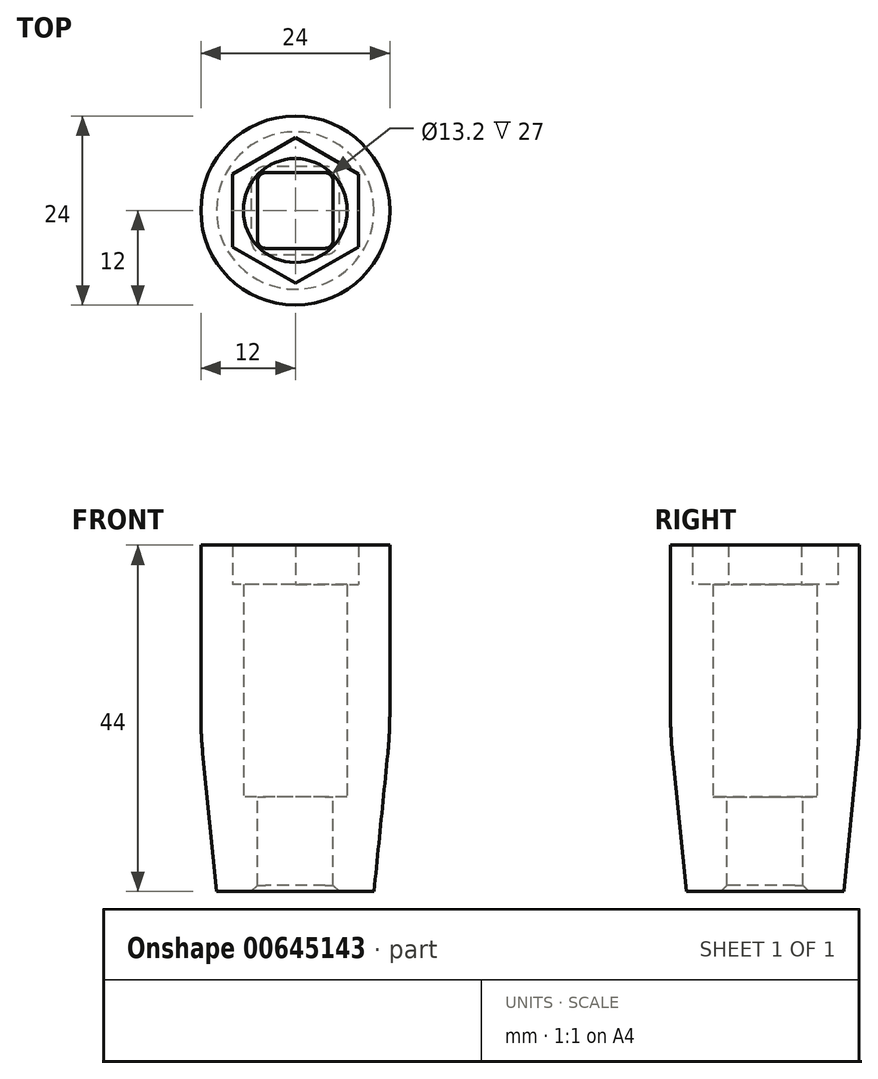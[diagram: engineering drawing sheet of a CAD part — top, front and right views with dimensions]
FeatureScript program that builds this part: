
annotation { "Feature Type Name" : "Feature", "Feature Type Description" : "" }
export const myFeature = defineFeature(function(context is Context, id is Id, definition is map)
    precondition{}
    {
        {
            var Q0;
            Q0=qCreatedBy(makeId("Top.planeOp"),FACE);
            var sketch = newSketch(context, id + "F0", { "sketchPlane" : qUnion([Q0])});
            skCircle(sketch, "E0.cCircle", {"center": v(0, 0) * mm, "radius": 8 * mm, "construction": true});
            skLineSegment(sketch, "E0.0", {"start": v(8, 4.62) * mm, "end": v(8, -4.62) * mm});
            skLineSegment(sketch, "E0.1", {"start": v(8, -4.62) * mm, "end": v(0, -9.24) * mm});
            skLineSegment(sketch, "E0.2", {"start": v(0, -9.24) * mm, "end": v(-8, -4.62) * mm});
            skLineSegment(sketch, "E0.3", {"start": v(-8, -4.62) * mm, "end": v(-8, 4.62) * mm});
            skLineSegment(sketch, "E0.4", {"start": v(-8, 4.62) * mm, "end": v(0, 9.24) * mm});
            skLineSegment(sketch, "E0.5", {"start": v(0, 9.24) * mm, "end": v(8, 4.62) * mm});
            skPoint(sketch, "E0.0.midPoint", {"position": v(8, 0) * mm});
            skCircle(sketch, "E1", {"center": v(0, 0) * mm, "radius": 12 * mm});
            skLineSegment(sketch, "E2.bottom", {"start": v(4.8, -4.8) * mm, "end": v(-4.8, -4.8) * mm});
            skLineSegment(sketch, "E2.top", {"start": v(4.8, 4.8) * mm, "end": v(-4.8, 4.8) * mm});
            skLineSegment(sketch, "E2.left", {"start": v(4.8, -4.8) * mm, "end": v(4.8, 4.8) * mm});
            skLineSegment(sketch, "E2.right", {"start": v(-4.8, -4.8) * mm, "end": v(-4.8, 4.8) * mm});
            skSolve(sketch);
        }
        {
            var Q0;
            {var subQ5=sQuery(id+"F0.wireOp",EDGE,"E0.0");Q0=makeQuery(id+"F0.imprint","IMPRINT",FACE,{"disambiguationData":[TD([[makeQuery(id+"F0.imprint","IMPRINT",EDGE,{"derivedFrom":subQ5}),1.0]])]});}
            var Q1;
            Q1=makeQuery(id+"F0.imprint","IMPRINT",FACE,{"disambiguationData":[TD([[makeQuery(id+"F0.imprint","IMPRINT",EDGE,{"derivedFrom":sQuery(id+"F0.wireOp",EDGE,"E1")}),-1.0]])]});
            extrude(context, id + "F1", {"entities" : qUnion([Q0, Q1]), "depth" : 32 * mm, "offsetDistance" : 25 * mm});
        }
        {
            var Q0;
            Q0=makeQuery(id+"F0.imprint","IMPRINT",FACE,{"disambiguationData":[TD([[makeQuery(id+"F0.imprint","IMPRINT",EDGE,{"derivedFrom":sQuery(id+"F0.wireOp",EDGE,"E0.0")}),-1.0]])]});
            var Q1;
            Q1=makeQuery(id+"F0.imprint","IMPRINT",FACE,{"disambiguationData":[TD([[makeQuery(id+"F0.imprint","IMPRINT",EDGE,{"derivedFrom":sQuery(id+"F0.wireOp",EDGE,"E0.0")}),1.0]])]});
            extrude(context, id + "F2", {"entities" : qUnion([Q0, Q1]), "operationType" : NewBodyOperationType.ADD, "oppositeDirection" : true, "depth" : 12 * mm, "offsetDistance" : 25 * mm});
        }
        {
            var Q0;
            Q0=makeQuery(id+"F2.opExtrude","CAP_EDGE",EDGE,{"disambiguationData":[OSD([sQuery(id+"F0.wireOp",EDGE,"E1")])],"isStart":false});
            chamfer(context, id + "F3", {"entities" : qUnion([Q0]), "chamferType" : ChamferType.TWO_OFFSETS, "width1" : 2 * mm, "oppositeDirection" : true, "width2" : 20 * mm, "tangentPropagation" : true});
        }
        {
            var Q0;
            Q0=makeQuery(id+"F2.opExtrude","SWEPT_EDGE",EDGE,{"disambiguationData":[OSD([sQuery(id+"F0.wireOp",EDGE,"E2.top"),sQuery(id+"F0.wireOp",EDGE,"E2.right")])]});
            var Q1;
            Q1=makeQuery(id+"F2.opExtrude","SWEPT_EDGE",EDGE,{"disambiguationData":[OSD([sQuery(id+"F0.wireOp",EDGE,"E2.top"),sQuery(id+"F0.wireOp",EDGE,"E2.left")])]});
            var Q2;
            Q2=makeQuery(id+"F2.opExtrude","SWEPT_EDGE",EDGE,{"disambiguationData":[OSD([sQuery(id+"F0.wireOp",EDGE,"E2.bottom"),sQuery(id+"F0.wireOp",EDGE,"E2.left")])]});
            var Q3;
            Q3=makeQuery(id+"F2.opExtrude","SWEPT_EDGE",EDGE,{"disambiguationData":[OSD([sQuery(id+"F0.wireOp",EDGE,"E2.bottom"),sQuery(id+"F0.wireOp",EDGE,"E2.right")])]});
            fillet(context, id + "F4", {"entities" : qUnion([Q0, Q1, Q2, Q3]), "tangentPropagation" : true, "radius" : 1 * mm, "defaultsChanged" : false, "vertexSettings" : [], "allowEdgeOverflow" : false});
        }
        {
            var Q0;
            Q0=makeQuery(id+"F0.imprint","IMPRINT",FACE,{"disambiguationData":[TD([[makeQuery(id+"F0.imprint","IMPRINT",EDGE,{"derivedFrom":sQuery(id+"F0.wireOp",EDGE,"E0.0")}),-1.0]])]});
            var sketch = newSketch(context, id + "F5", { "sketchPlane" : qUnion([Q0])});
            skCircle(sketch, "E3", {"center": v(0, 0) * mm, "radius": 6.6 * mm});
            skSolve(sketch);
        }
        {
            var Q0;
            {var subQ0=sQuery(id+"F5.wireOp",EDGE,"E3");var subQ1=makeQuery(id+"F0.imprint","IMPRINT",EDGE,{"derivedFrom":sQuery(id+"F0.wireOp",EDGE,"E2.top")});var subQ2=makeQuery(id+"F5.imprint","INTERSECT",VERTEX,{"disambiguationData":[OD(1.0)],"derivedFrom":[subQ1,subQ0]});Q0=makeQuery(id+"F5.imprint","IMPRINT",FACE,{"disambiguationData":[TD([[makeQuery(id+"F5.imprint","IMPRINT",EDGE,{"disambiguationData":[TD([[subQ2,-1.0]])],"derivedFrom":subQ0}),-1.0]])]});}
            var Q1;
            Q1=makeQuery(id+"F5.imprint","IMPRINT",FACE,{"disambiguationData":[TD([[makeQuery(id+"F5.imprint","IMPRINT",EDGE,{"derivedFrom":makeQuery(id+"F0.imprint","IMPRINT",EDGE,{"derivedFrom":sQuery(id+"F0.wireOp",EDGE,"E0.0")})}),-1.0]])]});
            var Q2;
            {var subQ0=sQuery(id+"F5.wireOp",EDGE,"E3");var subQ1=makeQuery(id+"F0.imprint","IMPRINT",EDGE,{"derivedFrom":sQuery(id+"F0.wireOp",EDGE,"E2.top")});var subQ2=makeQuery(id+"F5.imprint","INTERSECT",VERTEX,{"disambiguationData":[OD(0.0)],"derivedFrom":[subQ1,subQ0]});Q2=makeQuery(id+"F5.imprint","IMPRINT",FACE,{"disambiguationData":[TD([[makeQuery(id+"F5.imprint","IMPRINT",EDGE,{"disambiguationData":[TD([[subQ2,1.0]])],"derivedFrom":subQ0}),-1.0]])]});}
            var Q3;
            {var subQ0=sQuery(id+"F5.wireOp",EDGE,"E3");var subQ1=makeQuery(id+"F0.imprint","IMPRINT",EDGE,{"derivedFrom":sQuery(id+"F0.wireOp",EDGE,"E2.bottom")});var subQ2=makeQuery(id+"F5.imprint","INTERSECT",VERTEX,{"disambiguationData":[OD(1.0)],"derivedFrom":[subQ1,subQ0]});Q3=makeQuery(id+"F5.imprint","IMPRINT",FACE,{"disambiguationData":[TD([[makeQuery(id+"F5.imprint","IMPRINT",EDGE,{"disambiguationData":[TD([[subQ2,-1.0]])],"derivedFrom":subQ0}),-1.0]])]});}
            var Q4;
            {var subQ0=sQuery(id+"F5.wireOp",EDGE,"E3");var subQ1=makeQuery(id+"F0.imprint","IMPRINT",EDGE,{"derivedFrom":sQuery(id+"F0.wireOp",EDGE,"E2.right")});var subQ2=makeQuery(id+"F5.imprint","INTERSECT",VERTEX,{"disambiguationData":[OD(1.0)],"derivedFrom":[subQ1,subQ0]});Q4=makeQuery(id+"F5.imprint","IMPRINT",FACE,{"disambiguationData":[TD([[makeQuery(id+"F5.imprint","IMPRINT",EDGE,{"disambiguationData":[TD([[subQ2,-1.0]])],"derivedFrom":subQ0}),-1.0]])]});}
            extrude(context, id + "F6", {"entities" : qUnion([Q0, Q1, Q2, Q3, Q4]), "operationType" : NewBodyOperationType.ADD, "depth" : 27 * mm, "offsetDistance" : 25 * mm});
        }
        {
            var Q0;
            {var subQ0=sQuery(id+"F0.wireOp",EDGE,"E1");Q0=makeQuery(id+"F3.opChamfer","BLEND_EDGE",EDGE,{"blendedFrom":[makeQuery(id+"F2.opExtrude","CAP_EDGE",EDGE,{"disambiguationData":[OSD([subQ0])],"isStart":false}),makeQuery(id+"F2.boolean.opBoolean","MERGE",FACE,{"derivedFrom":[makeQuery(id+"F1.opExtrude","SWEPT_FACE",FACE,{"disambiguationData":[OSD([subQ0])]}),makeQuery(id+"F2.opExtrude","SWEPT_FACE",FACE,{"disambiguationData":[OSD([subQ0])]})]})],"blendedInto":[makeQuery(id+"F2.boolean.opBoolean","MERGE",FACE,{"derivedFrom":[makeQuery(id+"F1.opExtrude","SWEPT_FACE",FACE,{"disambiguationData":[OSD([subQ0])]}),makeQuery(id+"F2.opExtrude","SWEPT_FACE",FACE,{"disambiguationData":[OSD([subQ0])]})]})]});}
            fillet(context, id + "F7", {"entities" : qUnion([Q0]), "tangentPropagation" : true, "radius" : 50 * mm, "defaultsChanged" : true, "vertexSettings" : [], "allowEdgeOverflow" : false});
        }
        {
            var Q0;
            Q0=makeQuery(id+"F2.opExtrude","CAP_EDGE",EDGE,{"disambiguationData":[OSD([sQuery(id+"F0.wireOp",EDGE,"E2.bottom")])],"isStart":false});
            chamfer(context, id + "F8", {"entities" : qUnion([Q0]), "width" : 0.8 * mm, "tangentPropagation" : true});
        }
    });
